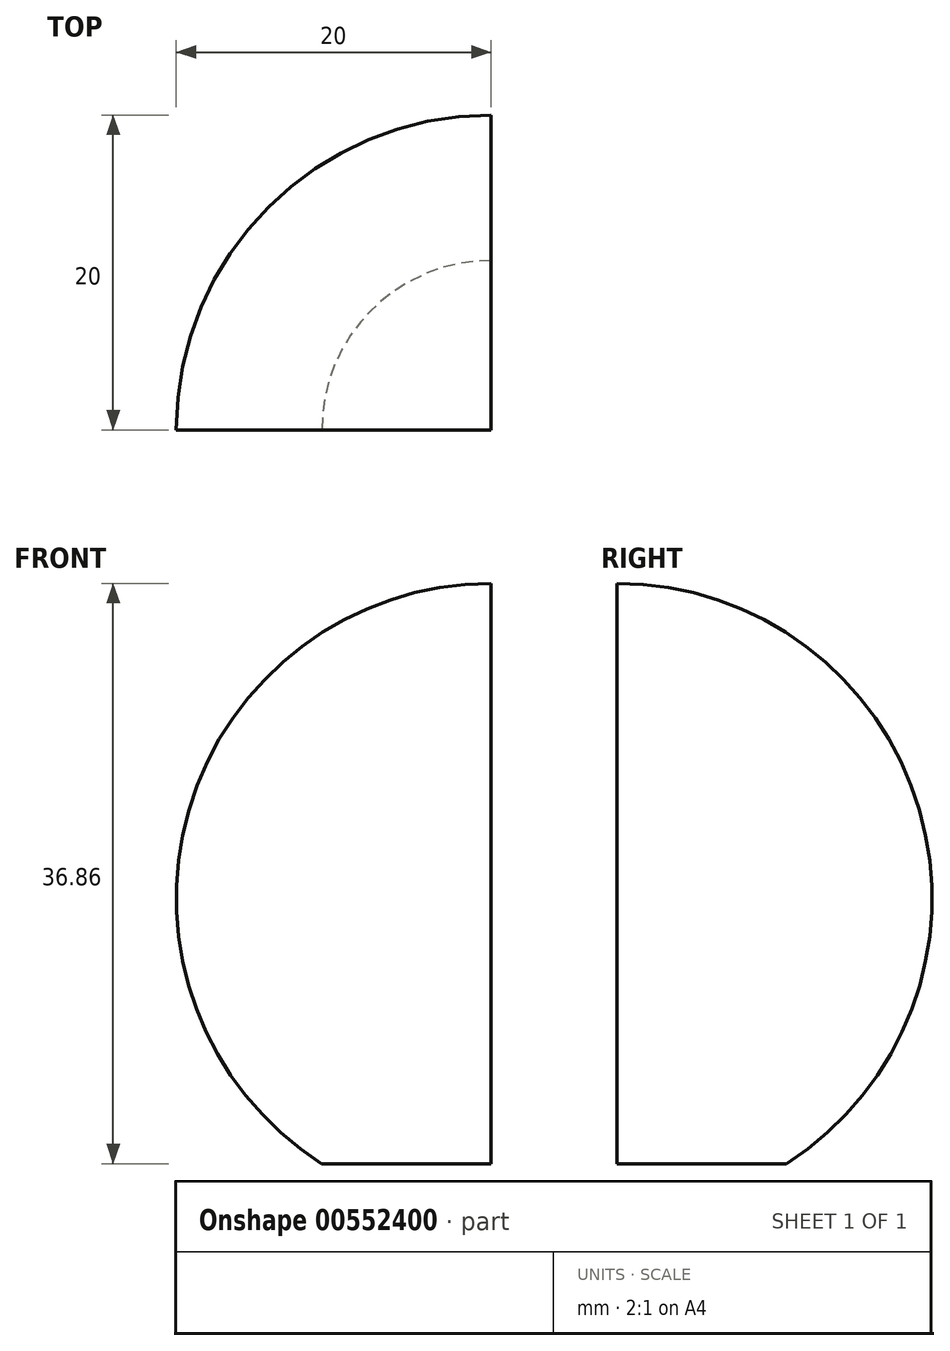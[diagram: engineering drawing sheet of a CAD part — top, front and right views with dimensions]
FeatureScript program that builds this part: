
annotation { "Feature Type Name" : "Feature", "Feature Type Description" : "" }
export const myFeature = defineFeature(function(context is Context, id is Id, definition is map)
    precondition{}
    {
        {
            var Q0;
            Q0=qCreatedBy(makeId("Front.planeOp"),FACE);
            var sketch = newSketch(context, id + "F0", { "sketchPlane" : qUnion([Q0])});
            skArc(sketch, "E0", {"start": v(0, 20) * mm, "mid": v(-19.2, 5.6) * mm, "end": v(-10.76, -16.86) * mm});
            skLineSegment(sketch, "E1", {"start": v(0, 20) * mm, "end": v(0, -16.86) * mm});
            skLineSegment(sketch, "E2", {"start": v(0, -16.86) * mm, "end": v(-10.76, -16.86) * mm});
            skPoint(sketch, "E3.orphan", {"position": v(0, 22.81) * mm});
            skSolve(sketch);
        }
        {
            var Q0;
            Q0=makeQuery(id+"F0.imprint","IMPRINT",FACE,{"disambiguationData":[TD([[makeQuery(id+"F0.imprint","IMPRINT",EDGE,{"derivedFrom":sQuery(id+"F0.wireOp",EDGE,"E0")}),1.0]])]});
            var Q1;
            Q1=sQuery(id+"F0.wireOp",EDGE,"E1");
            revolve(context, id + "F1", {"entities" : qUnion([Q0]), "axis" : qUnion([Q1]), "revolveType" : RevolveType.ONE_DIRECTION, "angle" : 90 * degree});
        }
    });
